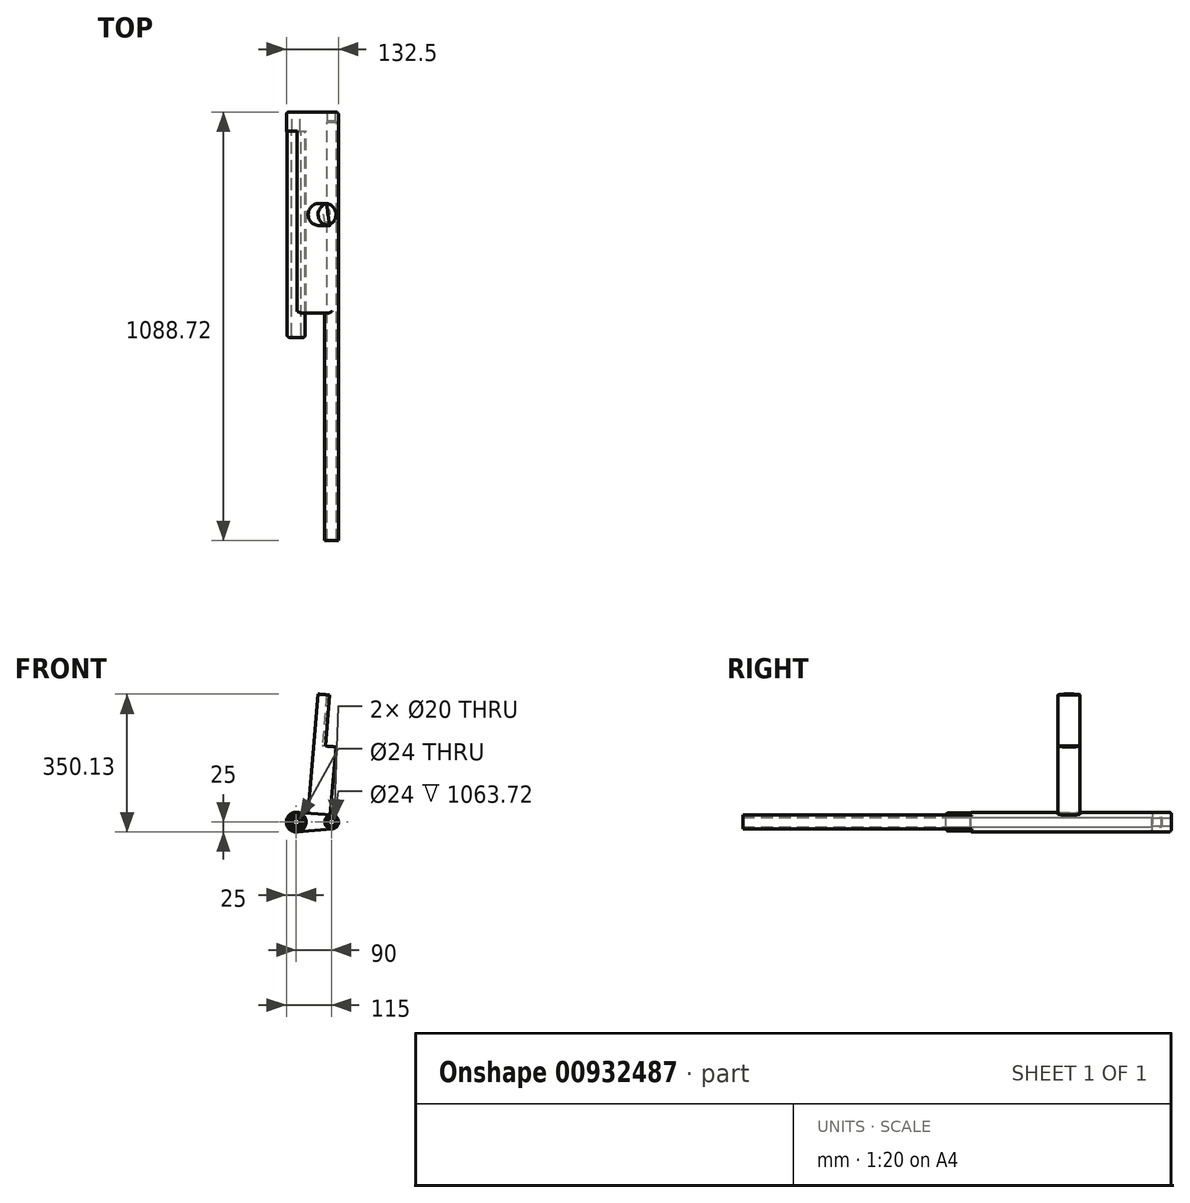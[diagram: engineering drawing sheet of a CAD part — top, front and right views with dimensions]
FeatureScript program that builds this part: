
annotation { "Feature Type Name" : "Feature", "Feature Type Description" : "" }
export const myFeature = defineFeature(function(context is Context, id is Id, definition is map)
    precondition{}
    {
        {
            var Q0;
            Q0=qCreatedBy(makeId("Front.planeOp"),FACE);
            var sketch = newSketch(context, id + "F0", { "sketchPlane" : qUnion([Q0])});
            skCircle(sketch, "E0", {"center": v(0, 0) * mm, "radius": 25 * mm});
            skCircle(sketch, "E1", {"center": v(90, 0) * mm, "radius": 17.5 * mm});
            skLineSegment(sketch, "E2", {"start": v(2.08, 24.91) * mm, "end": v(91.46, 17.44) * mm});
            skLineSegment(sketch, "E3", {"start": v(2.08, -24.91) * mm, "end": v(91.46, -17.44) * mm});
            skCircle(sketch, "E4", {"center": v(0, 0) * mm, "radius": 10 * mm});
            skCircle(sketch, "E5", {"center": v(90, 0) * mm, "radius": 10 * mm});
            skSolve(sketch);
        }
        {
            var Q0;
            Q0=qSketchRegion(id+"F0",true);
            extrude(context, id + "F1", {"entities" : qUnion([Q0]), "depth" : 25 * mm});
        }
        {
            var Q0;
            Q0=makeQuery(id+"F0.imprint","IMPRINT",FACE,{"disambiguationData":[TD([[makeQuery(id+"F0.imprint","IMPRINT",EDGE,{"derivedFrom":sQuery(id+"F0.wireOp",EDGE,"E4")}),-1.0]])]});
            extrude(context, id + "F2", {"entities" : qUnion([Q0]), "operationType" : NewBodyOperationType.ADD, "depth" : 50 * mm});
        }
        {
            var Q0;
            Q0=makeQuery(id+"F2.opExtrude","CAP_EDGE",EDGE,{"disambiguationData":[OSD([sQuery(id+"F0.wireOp",EDGE,"E0")])],"isStart":false});
            var Q1;
            Q1=makeQuery(id+"F2.opExtrude","CAP_EDGE",EDGE,{"disambiguationData":[OSD([sQuery(id+"F0.wireOp",EDGE,"E4")])],"isStart":false});
            var Q2;
            Q2=makeQuery(id+"F1.opExtrude","CAP_EDGE",EDGE,{"disambiguationData":[OSD([sQuery(id+"F0.wireOp",EDGE,"E5")])],"isStart":false});
            chamfer(context, id + "F3", {"entities" : qUnion([Q0, Q1, Q2]), "width" : 2 * mm, "tangentPropagation" : true});
        }
        {
            var Q0;
            Q0=makeQuery(id+"F2.opExtrude","CAP_FACE",FACE,{"disambiguationData":[OSD([sQuery(id+"F0.wireOp",EDGE,"E0"),sQuery(id+"F0.wireOp",EDGE,"E4")])],"isStart":false});
            extrude(context, id + "F4", {"entities" : qUnion([Q0]), "operationType" : NewBodyOperationType.ADD, "depth" : 76.47 * mm, "offsetDistance" : 25 * mm});
        }
        {
            var Q0;
            {var subQ0=sQuery(id+"F0.wireOp",EDGE,"E2");Q0=makeQuery(id+"F0.imprint","IMPRINT",FACE,{"disambiguationData":[TD([[makeQuery(id+"F0.imprint","IMPRINT",EDGE,{"derivedFrom":subQ0}),-1.0]])]});}
            extrude(context, id + "F5", {"entities" : qUnion([Q0]), "operationType" : NewBodyOperationType.ADD, "depth" : 511.24 * mm, "offsetDistance" : 25 * mm});
        }
        {
            var Q0;
            Q0=makeQuery(id+"F4.opExtrude","CAP_FACE",FACE,{"disambiguationData":[OSD([sQuery(id+"F0.wireOp",EDGE,"E0"),sQuery(id+"F0.wireOp",EDGE,"E4")])],"isStart":false});
            extrude(context, id + "F6", {"entities" : qUnion([Q0]), "operationType" : NewBodyOperationType.ADD, "depth" : 446.14 * mm, "offsetDistance" : 25 * mm});
        }
        {
            var Q0;
            Q0=makeQuery(id+"F1.opExtrude","CAP_FACE",FACE,{"disambiguationData":[OSD([sQuery(id+"F0.wireOp",EDGE,"E0"),sQuery(id+"F0.wireOp",EDGE,"E1"),sQuery(id+"F0.wireOp",EDGE,"E2"),sQuery(id+"F0.wireOp",EDGE,"E3"),sQuery(id+"F0.wireOp",EDGE,"E4"),sQuery(id+"F0.wireOp",EDGE,"E5")])],"isStart":false});
            extrude(context, id + "F7", {"entities" : qUnion([Q0]), "operationType" : NewBodyOperationType.ADD, "depth" : 1063.72 * mm, "offsetDistance" : 25 * mm});
        }
        {
            var Q0;
            Q0=makeQuery(id+"F5.opExtrude","CAP_EDGE",EDGE,{"disambiguationData":[OSD([sQuery(id+"F0.wireOp",EDGE,"E2")])],"isStart":false});
            var Q1;
            Q1=makeQuery(id+"F5.opExtrude","CAP_EDGE",EDGE,{"disambiguationData":[OSD([sQuery(id+"F0.wireOp",EDGE,"E3")])],"isStart":false});
            fillet(context, id + "F8", {"entities" : qUnion([Q0, Q1]), "radius" : 5 * mm, "tangentPropagation" : true, "allowEdgeOverflow" : false});
        }
        {
            var Q0;
            {var subQ0=sQuery(id+"F0.wireOp",EDGE,"E4");var subQ1=sQuery(id+"F0.wireOp",EDGE,"E0");Q0=makeQuery(id+"F6.opExtrude","CAP_EDGE",EDGE,{"disambiguationData":[OSD([subQ1,subQ0]),TDD([makeQuery(id+"F4.opExtrude","CAP_EDGE",EDGE,{"disambiguationData":[OSD([subQ1,subQ0]),TDD([makeQuery(id+"F3.opChamfer","BLEND_EDGE",EDGE,{"blendedFrom":[makeQuery(id+"F2.opExtrude","CAP_EDGE",EDGE,{"disambiguationData":[OSD([subQ1])],"isStart":false}),makeQuery(id+"F2.opExtrude","CAP_FACE",FACE,{"disambiguationData":[OSD([subQ1,subQ0])],"isStart":false})],"blendedInto":[makeQuery(id+"F2.opExtrude","CAP_FACE",FACE,{"disambiguationData":[OSD([subQ1,subQ0])],"isStart":false})]})])],"isStart":false})])],"isStart":false});}
            fillet(context, id + "F9", {"entities" : qUnion([Q0]), "radius" : 6.2 * mm, "tangentPropagation" : true, "allowEdgeOverflow" : false});
        }
        {
            var Q0;
            {var subQ0=sQuery(id+"F0.wireOp",EDGE,"E4");var subQ1=sQuery(id+"F0.wireOp",EDGE,"E0");Q0=makeQuery(id+"F6.opExtrude","CAP_EDGE",EDGE,{"disambiguationData":[OSD([subQ1,subQ0]),TDD([makeQuery(id+"F4.opExtrude","CAP_EDGE",EDGE,{"disambiguationData":[OSD([subQ1,subQ0]),TDD([makeQuery(id+"F3.opChamfer","BLEND_EDGE",EDGE,{"blendedFrom":[makeQuery(id+"F2.opExtrude","CAP_EDGE",EDGE,{"disambiguationData":[OSD([subQ0])],"isStart":false}),makeQuery(id+"F2.opExtrude","CAP_FACE",FACE,{"disambiguationData":[OSD([subQ1,subQ0])],"isStart":false})],"blendedInto":[makeQuery(id+"F2.opExtrude","CAP_FACE",FACE,{"disambiguationData":[OSD([subQ1,subQ0])],"isStart":false})]})])],"isStart":false})])],"isStart":false});}
            fillet(context, id + "F10", {"entities" : qUnion([Q0]), "radius" : 6.9 * mm, "tangentPropagation" : true, "allowEdgeOverflow" : false});
        }
        {
            var Q0;
            Q0=makeQuery(id+"F1.opExtrude","CAP_EDGE",EDGE,{"disambiguationData":[OSD([sQuery(id+"F0.wireOp",EDGE,"E0")])],"isStart":true});
            fillet(context, id + "F11", {"entities" : qUnion([Q0]), "radius" : 6.6 * mm, "tangentPropagation" : true, "allowEdgeOverflow" : false});
        }
        {
            var Q0;
            {var subQ0=sQuery(id+"F0.wireOp",EDGE,"E4");var subQ1=sQuery(id+"F0.wireOp",EDGE,"E0");var subQ2=makeQuery(id+"F3.opChamfer","BLEND_EDGE",EDGE,{"blendedFrom":[makeQuery(id+"F2.opExtrude","CAP_EDGE",EDGE,{"disambiguationData":[OSD([subQ1])],"isStart":false}),makeQuery(id+"F2.opExtrude","CAP_FACE",FACE,{"disambiguationData":[OSD([subQ1,subQ0])],"isStart":false})],"blendedInto":[makeQuery(id+"F2.opExtrude","CAP_FACE",FACE,{"disambiguationData":[OSD([subQ1,subQ0])],"isStart":false})]});Q0=makeQuery(id+"F4.boolean.opBoolean","MERGE",EDGE,{"derivedFrom":[subQ2,makeQuery(id+"F4.opExtrude","CAP_EDGE",EDGE,{"disambiguationData":[OSD([subQ1,subQ0]),TDD([subQ2])],"isStart":true})]});}
            fillet(context, id + "F12", {"entities" : qUnion([Q0]), "radius" : 7.2 * mm, "tangentPropagation" : true, "allowEdgeOverflow" : false});
        }
        {
            var Q0;
            {var subQ0=sQuery(id+"F0.wireOp",EDGE,"E2");Q0=makeQuery(id+"F5.boolean.opBoolean","MERGE",FACE,{"derivedFrom":[makeQuery(id+"F1.opExtrude","SWEPT_FACE",FACE,{"disambiguationData":[OSD([subQ0])]}),makeQuery(id+"F5.opExtrude","SWEPT_FACE",FACE,{"disambiguationData":[OSD([subQ0])]})]});}
            var sketch = newSketch(context, id + "F13", { "sketchPlane" : qUnion([Q0])});
            skCircle(sketch, "E6", {"center": v(56.59, -260.31) * mm, "radius": 28.16 * mm});
            skSolve(sketch);
        }
        {
            var Q0;
            Q0 = qSketchRegion(id + "F13", true);
            extrude(context, id + "F14", {"entities" : qUnion([Q0]), "operationType" : NewBodyOperationType.ADD, "depth" : 173.64 * mm, "offsetDistance" : 25 * mm});
        }
        {
            var Q0;
            Q0=makeQuery(id+"F14.opExtrude","CAP_FACE",FACE,{"disambiguationData":[OSD([sQuery(id+"F13.wireOp",EDGE,"E6")])],"isStart":false});
            var sketch = newSketch(context, id + "F15", { "sketchPlane" : qUnion([Q0])});
            skLineSegment(sketch, "E7", {"start": v(57.95, -288.44) * mm, "end": v(49.38, -233.09) * mm});
            skSolve(sketch);
        }
        {
            var Q0;
            Q0 = qSketchRegion(id + "F15", true);
            var Q1;
            {var subQ0=sQuery(id+"F15.wireOp",EDGE,"E7");Q1=makeQuery(id+"F15.imprint","IMPRINT",FACE,{"disambiguationData":[TD([[makeQuery(id+"F15.imprint","IMPRINT",EDGE,{"derivedFrom":subQ0}),1.0]])]});}
            extrude(context, id + "F16", {"entities" : qUnion([Q0, Q1]), "operationType" : NewBodyOperationType.ADD, "depth" : 130 * mm, "offsetDistance" : 25 * mm});
        }
    });
